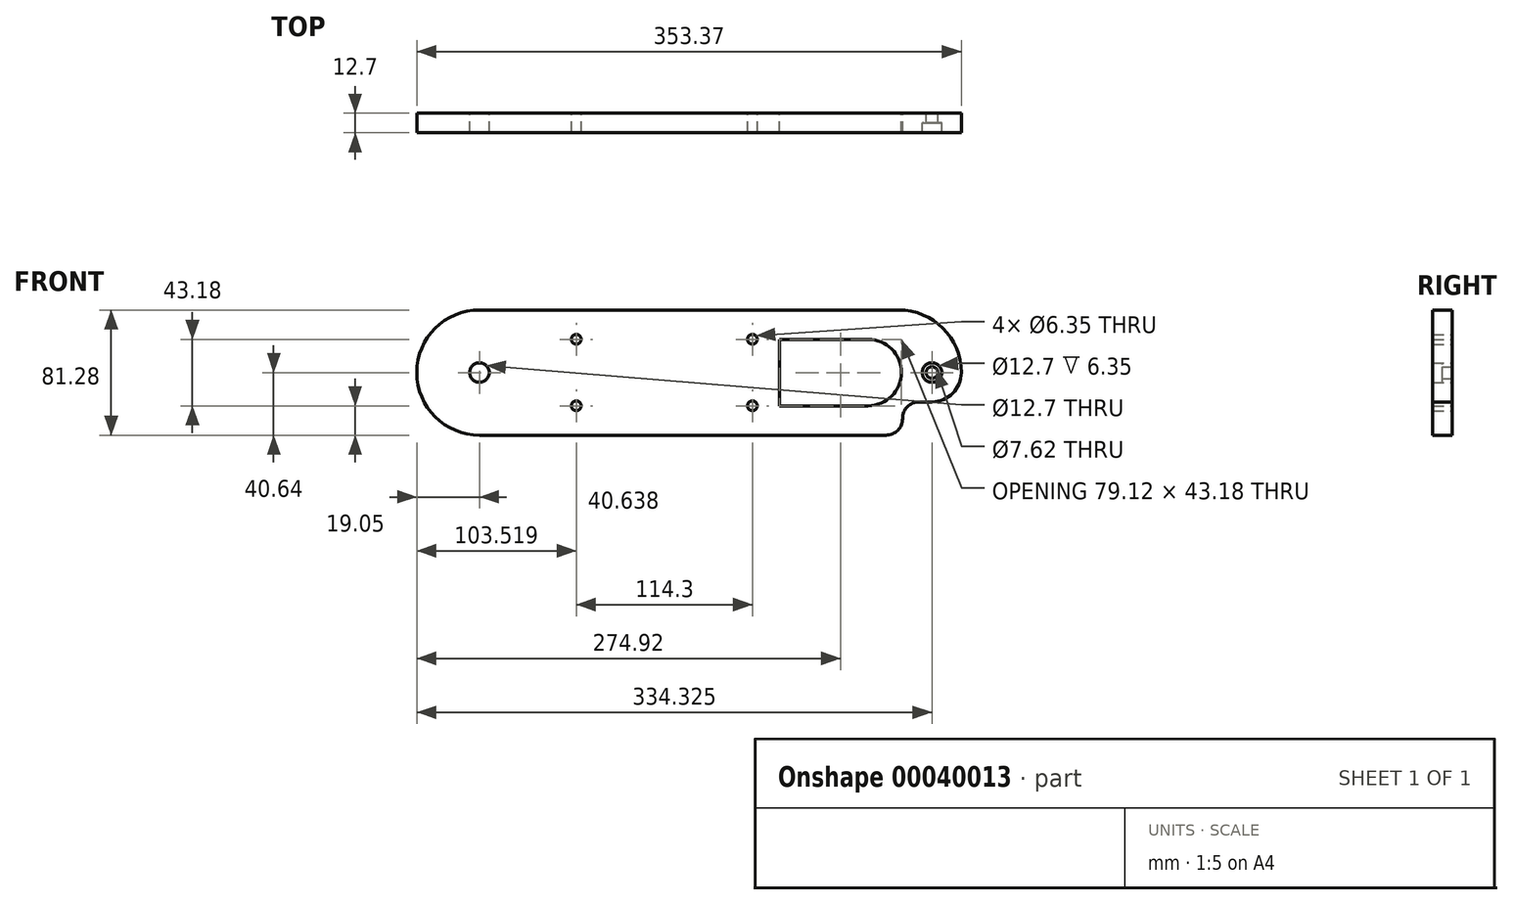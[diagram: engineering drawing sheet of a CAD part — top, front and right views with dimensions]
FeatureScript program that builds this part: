
annotation { "Feature Type Name" : "Feature", "Feature Type Description" : "" }
export const myFeature = defineFeature(function(context is Context, id is Id, definition is map)
    precondition{}
    {
        {
            var Q0;
            Q0=qCreatedBy(makeId("Front.planeOp"),FACE);
            var sketch = newSketch(context, id + "F0", { "sketchPlane" : qUnion([Q0])});
            skArc(sketch, "E0", {"start": v(-40.95, 11) * mm, "mid": v(-40.85, 11) * mm, "end": v(-40.74, 11) * mm});
            skArc(sketch, "E1.cCircle", {"start": v(-40.95, 11) * mm, "mid": v(-40.85, 11) * mm, "end": v(-40.74, 11) * mm, "construction": true});
            skCircle(sketch, "E2", {"center": v(-352.21, -56.94) * mm, "radius": 3.18 * mm});
            skLineSegment(sketch, "E3", {"start": v(-80.77, -78.53) * mm, "end": v(-80.77, -78.53) * mm});
            skCircle(sketch, "E4", {"center": v(-121.4, -78.53) * mm, "radius": 3.81 * mm});
            skArc(sketch, "E5.filletArc", {"start": v(-129.66, -97.58) * mm, "mid": v(-137.3, -100.74) * mm, "end": v(-140.46, -108.37) * mm});
            skArc(sketch, "E6.filletArc", {"start": v(-151.25, -119.17) * mm, "mid": v(-143.62, -116) * mm, "end": v(-140.46, -108.37) * mm});
            skPoint(sketch, "E7.visualSharp", {"position": v(-123, -37.89) * mm});
            skPoint(sketch, "E8", {"position": v(-123, -97.58) * mm});
            skPoint(sketch, "E9.visualSharp", {"position": v(-141.73, -37.89) * mm});
            skPoint(sketch, "E10", {"position": v(-121.4, -119.17) * mm});
            skPoint(sketch, "E11.visualSharp", {"position": v(-102.36, -37.89) * mm});
            skPoint(sketch, "E5.visualSharp", {"position": v(-140.46, -97.58) * mm});
            skLineSegment(sketch, "E12.left", {"start": v(-102.36, -78.53) * mm, "end": v(-102.36, -78.53) * mm});
            skCircle(sketch, "E13", {"center": v(-352.21, -100.12) * mm, "radius": 3.18 * mm});
            skLineSegment(sketch, "E14.bottom", {"start": v(-415.1, -37.89) * mm, "end": v(-150.15, -37.89) * mm});
            skLineSegment(sketch, "E14.top", {"start": v(-415.1, -119.17) * mm, "end": v(-151.25, -119.17) * mm});
            skLineSegment(sketch, "E14.left", {"start": v(-415.1, -37.89) * mm, "end": v(-415.1, -119.17) * mm});
            skPoint(sketch, "E15.visualSharp", {"position": v(-123, -119.17) * mm});
            skArc(sketch, "E16", {"start": v(-415.1, -37.89) * mm, "mid": v(-455.73, -78.53) * mm, "end": v(-415.1, -119.17) * mm});
            skCircle(sketch, "E17", {"center": v(-237.91, -56.94) * mm, "radius": 3.18 * mm});
            skLineSegment(sketch, "E18", {"start": v(-123, -97.58) * mm, "end": v(-140.46, -97.58) * mm});
            skCircle(sketch, "E19", {"center": v(-415.1, -78.53) * mm, "radius": 3.81 * mm});
            skPoint(sketch, "E20", {"position": v(-123, -78.53) * mm});
            skCircle(sketch, "E21", {"center": v(-121.4, -78.53) * mm, "radius": 6.35 * mm});
            skCircle(sketch, "E22", {"center": v(-415.1, -78.53) * mm, "radius": 6.35 * mm});
            skArc(sketch, "E11.filletArc", {"start": v(-102.36, -78.53) * mm, "mid": v(-114.26, -49.8) * mm, "end": v(-143, -37.89) * mm});
            skArc(sketch, "E23", {"start": v(-121.4, -97.58) * mm, "mid": v(-107.93, -92) * mm, "end": v(-102.36, -78.53) * mm});
            skPoint(sketch, "E24.visualSharp", {"position": v(-80.77, -97.58) * mm});
            skPoint(sketch, "E25.visualSharp", {"position": v(-139.36, -59.48) * mm});
            skPoint(sketch, "E6.visualSharp", {"position": v(-140.46, -119.17) * mm});
            skPoint(sketch, "E26", {"position": v(-123, -59.48) * mm});
            skCircle(sketch, "E27", {"center": v(-237.91, -100.12) * mm, "radius": 3.18 * mm});
            skLineSegment(sketch, "E28", {"start": v(-140.46, -108.37) * mm, "end": v(-140.46, -108.37) * mm});
            skLineSegment(sketch, "E29", {"start": v(-140.46, -97.58) * mm, "end": v(-123, -97.58) * mm});
            skPoint(sketch, "E30", {"position": v(-102.36, -37.83) * mm});
            skLineSegment(sketch, "E31", {"start": v(-150.15, -37.89) * mm, "end": v(-141.73, -37.89) * mm});
            skLineSegment(sketch, "E32", {"start": v(-123, -37.89) * mm, "end": v(-121.4, -37.89) * mm});
            skLineSegment(sketch, "E33.trimOffspring", {"start": v(-129.66, -97.58) * mm, "end": v(-121.4, -97.58) * mm});
            skLineSegment(sketch, "E12.top", {"start": v(-141.73, -37.89) * mm, "end": v(-143, -37.89) * mm});
            skPoint(sketch, "E34.center.orphan", {"position": v(-185.44, -79.56) * mm});
            skArc(sketch, "E35", {"start": v(-162.84, -100.12) * mm, "mid": v(-141.25, -78.53) * mm, "end": v(-162.84, -56.94) * mm});
            skLineSegment(sketch, "E36.top", {"start": v(-220.37, -100.12) * mm, "end": v(-162.84, -100.12) * mm});
            skLineSegment(sketch, "E36.left", {"start": v(-220.37, -56.94) * mm, "end": v(-220.37, -100.12) * mm});
            skLineSegment(sketch, "E36.bottom", {"start": v(-220.37, -56.94) * mm, "end": v(-162.84, -56.94) * mm});
            skPoint(sketch, "E37", {"position": v(-162.8, -78.53) * mm});
            skSolve(sketch);
        }
        {
            var Q0;
            Q0 = qSketchRegion(id + "F0", true);
            extrude(context, id + "F1", {"entities" : qUnion([Q0]), "depth" : 12.7 * mm});
        }
        {
            var Q0;
            {var subQ0=sQuery(id+"F0.wireOp",EDGE,"E22");var subQ1=sQuery(id+"F0.wireOp",EDGE,"E14.left");var subQ3=makeQuery(id+"F0.imprint","INTERSECT",VERTEX,{"disambiguationData":[OD(0.0)],"derivedFrom":[subQ1,subQ0]});Q0=makeQuery(id+"F0.imprint","IMPRINT",FACE,{"disambiguationData":[TD([[makeQuery(id+"F0.imprint","IMPRINT",EDGE,{"disambiguationData":[TD([[subQ3,-1.0]])],"derivedFrom":subQ1}),-1.0]])]});}
            var Q1;
            {var subQ0=sQuery(id+"F0.wireOp",EDGE,"E22");var subQ1=sQuery(id+"F0.wireOp",EDGE,"E14.left");var subQ3=makeQuery(id+"F0.imprint","INTERSECT",VERTEX,{"disambiguationData":[OD(0.0)],"derivedFrom":[subQ1,subQ0]});Q1=makeQuery(id+"F0.imprint","IMPRINT",FACE,{"disambiguationData":[TD([[makeQuery(id+"F0.imprint","IMPRINT",EDGE,{"disambiguationData":[TD([[subQ3,-1.0]])],"derivedFrom":subQ1}),1.0]])]});}
            extrude(context, id + "F2", {"entities" : qUnion([Q0, Q1]), "operationType" : NewBodyOperationType.ADD, "depth" : 6.35 * mm});
        }
        {
            var Q0;
            Q0=makeQuery(id+"F0.imprint","IMPRINT",FACE,{"disambiguationData":[TD([[makeQuery(id+"F0.imprint","IMPRINT",EDGE,{"derivedFrom":sQuery(id+"F0.wireOp",EDGE,"E4")}),-1.0]])]});
            extrude(context, id + "F3", {"entities" : qUnion([Q0]), "operationType" : NewBodyOperationType.ADD, "depth" : 6.35 * mm});
        }
    });
